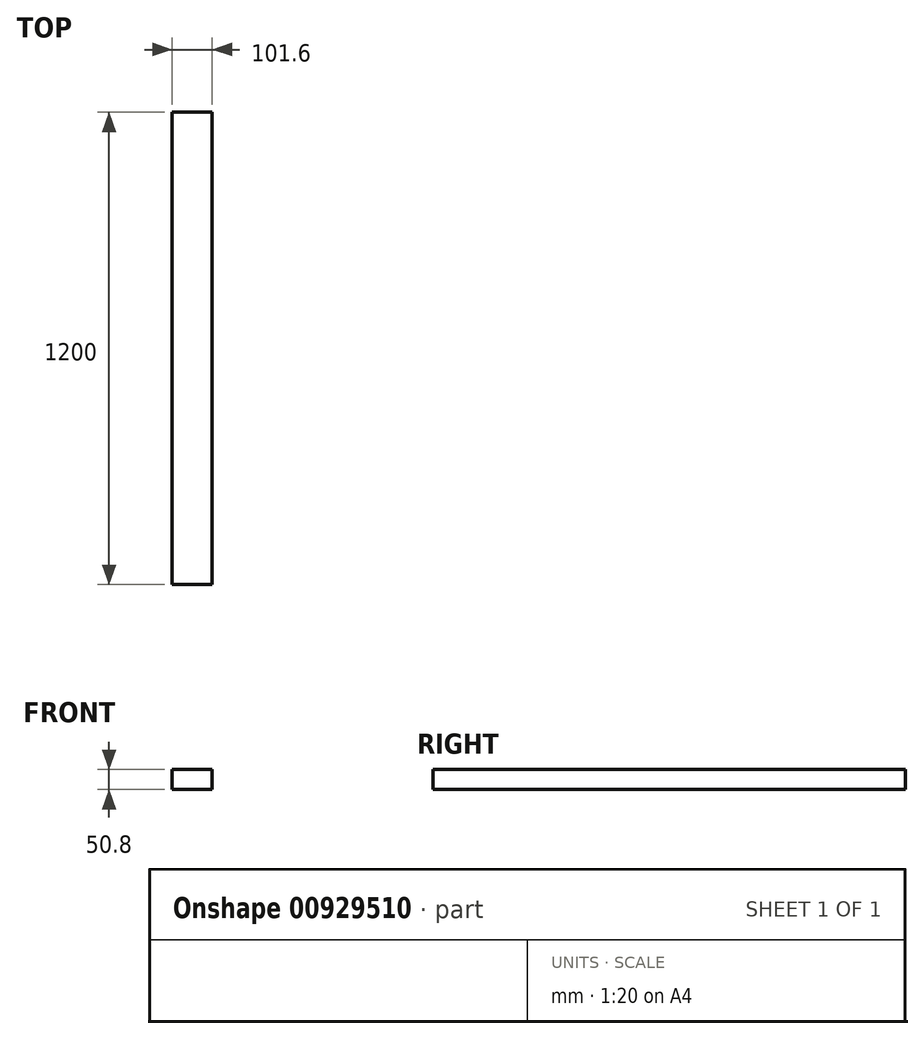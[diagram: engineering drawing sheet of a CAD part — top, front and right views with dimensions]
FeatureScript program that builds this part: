
annotation { "Feature Type Name" : "Feature", "Feature Type Description" : "" }
export const myFeature = defineFeature(function(context is Context, id is Id, definition is map)
    precondition{}
    {
        {
            var Q0;
            Q0=qCreatedBy(makeId("Front.planeOp"),FACE);
            var sketch = newSketch(context, id + "F0", { "sketchPlane" : qUnion([Q0])});
            skLineSegment(sketch, "E0", {"start": v(0, 0) * mm, "end": v(50.8, 0) * mm});
            skLineSegment(sketch, "E1", {"start": v(0, 0) * mm, "end": v(-50.8, 0) * mm});
            skLineSegment(sketch, "E2", {"start": v(50.8, 0) * mm, "end": v(50.8, 50.8) * mm});
            skLineSegment(sketch, "E3", {"start": v(-50.8, 0) * mm, "end": v(-50.8, 50.8) * mm});
            skLineSegment(sketch, "E4", {"start": v(-50.8, 50.8) * mm, "end": v(50.8, 50.8) * mm});
            skSolve(sketch);
        }
        {
            var Q0;
            Q0=makeQuery(id+"F0.imprint","IMPRINT",FACE,{"disambiguationData":[TD([[makeQuery(id+"F0.imprint","IMPRINT",EDGE,{"derivedFrom":sQuery(id+"F0.wireOp",EDGE,"E0")}),1.0]])]});
            extrude(context, id + "F1", {"entities" : qUnion([Q0]), "endBound" : BoundingType.SYMMETRIC, "depth" : 1200 * mm, "offsetDistance" : 25 * mm});
        }
    });
